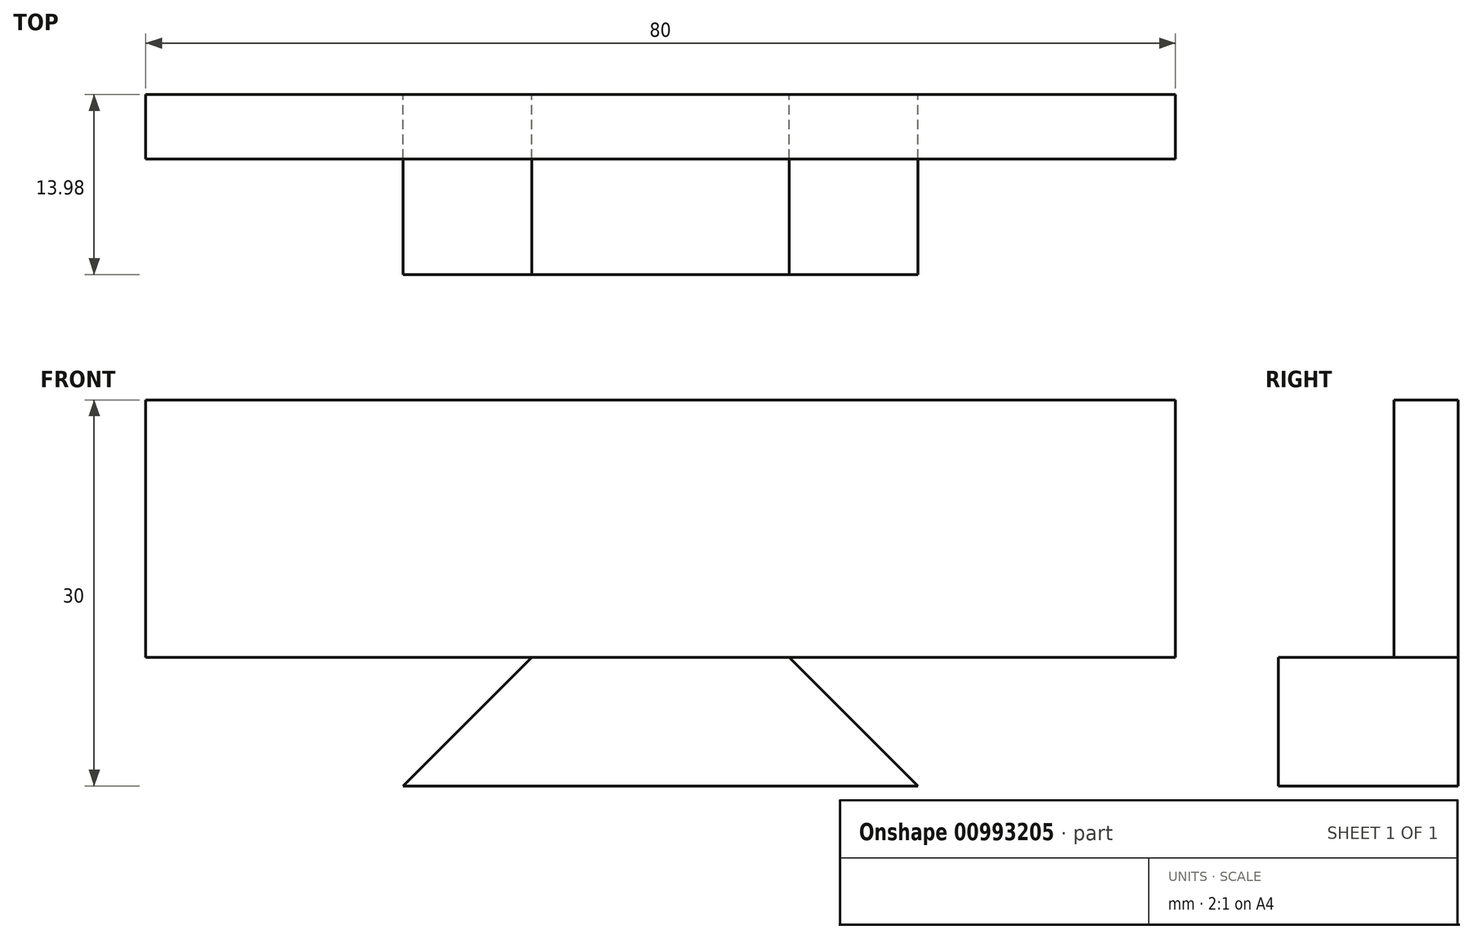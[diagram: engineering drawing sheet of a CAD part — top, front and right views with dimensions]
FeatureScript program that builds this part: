
annotation { "Feature Type Name" : "Feature", "Feature Type Description" : "" }
export const myFeature = defineFeature(function(context is Context, id is Id, definition is map)
    precondition{}
    {
        {
            var Q0;
            Q0=qCreatedBy(makeId("Front.planeOp"),FACE);
            var sketch = newSketch(context, id + "F0", { "sketchPlane" : qUnion([Q0])});
            skLineSegment(sketch, "E0.bottom", {"start": v(40, -10) * mm, "end": v(-40, -10) * mm});
            skLineSegment(sketch, "E0.top", {"start": v(40, 10) * mm, "end": v(-40, 10) * mm});
            skLineSegment(sketch, "E0.left", {"start": v(40, -10) * mm, "end": v(40, 10) * mm});
            skLineSegment(sketch, "E0.right", {"start": v(-40, -10) * mm, "end": v(-40, 10) * mm});
            skPoint(sketch, "E0.middle", {"position": v(0, 0) * mm});
            skSolve(sketch);
        }
        {
            var Q0;
            Q0 = qSketchRegion(id + "F0", true);
            extrude(context, id + "F1", {"entities" : qUnion([Q0]), "depth" : 5 * mm, "offsetDistance" : 25 * mm});
        }
        {
            var Q0;
            Q0=qCreatedBy(makeId("Front.planeOp"),FACE);
            var sketch = newSketch(context, id + "F2", { "sketchPlane" : qUnion([Q0])});
            skLineSegment(sketch, "E1.top", {"start": v(0, -20) * mm, "end": v(-20, -20) * mm});
            skLineSegment(sketch, "E2.top", {"start": v(0, -20) * mm, "end": v(20, -20) * mm});
            skLineSegment(sketch, "E2.left", {"start": v(0, -10) * mm, "end": v(0, -20) * mm});
            skLineSegment(sketch, "E3", {"start": v(-20, -20) * mm, "end": v(-10, -10) * mm});
            skLineSegment(sketch, "E4", {"start": v(-10, -10) * mm, "end": v(10, -10) * mm});
            skLineSegment(sketch, "E5", {"start": v(10, -10) * mm, "end": v(20, -20) * mm});
            skSolve(sketch);
        }
        {
            var Q0;
            Q0 = qSketchRegion(id + "F2", true);
            extrude(context, id + "F3", {"entities" : qUnion([Q0]), "operationType" : NewBodyOperationType.ADD, "depth" : 13.98 * mm, "offsetDistance" : 25 * mm});
        }
    });
